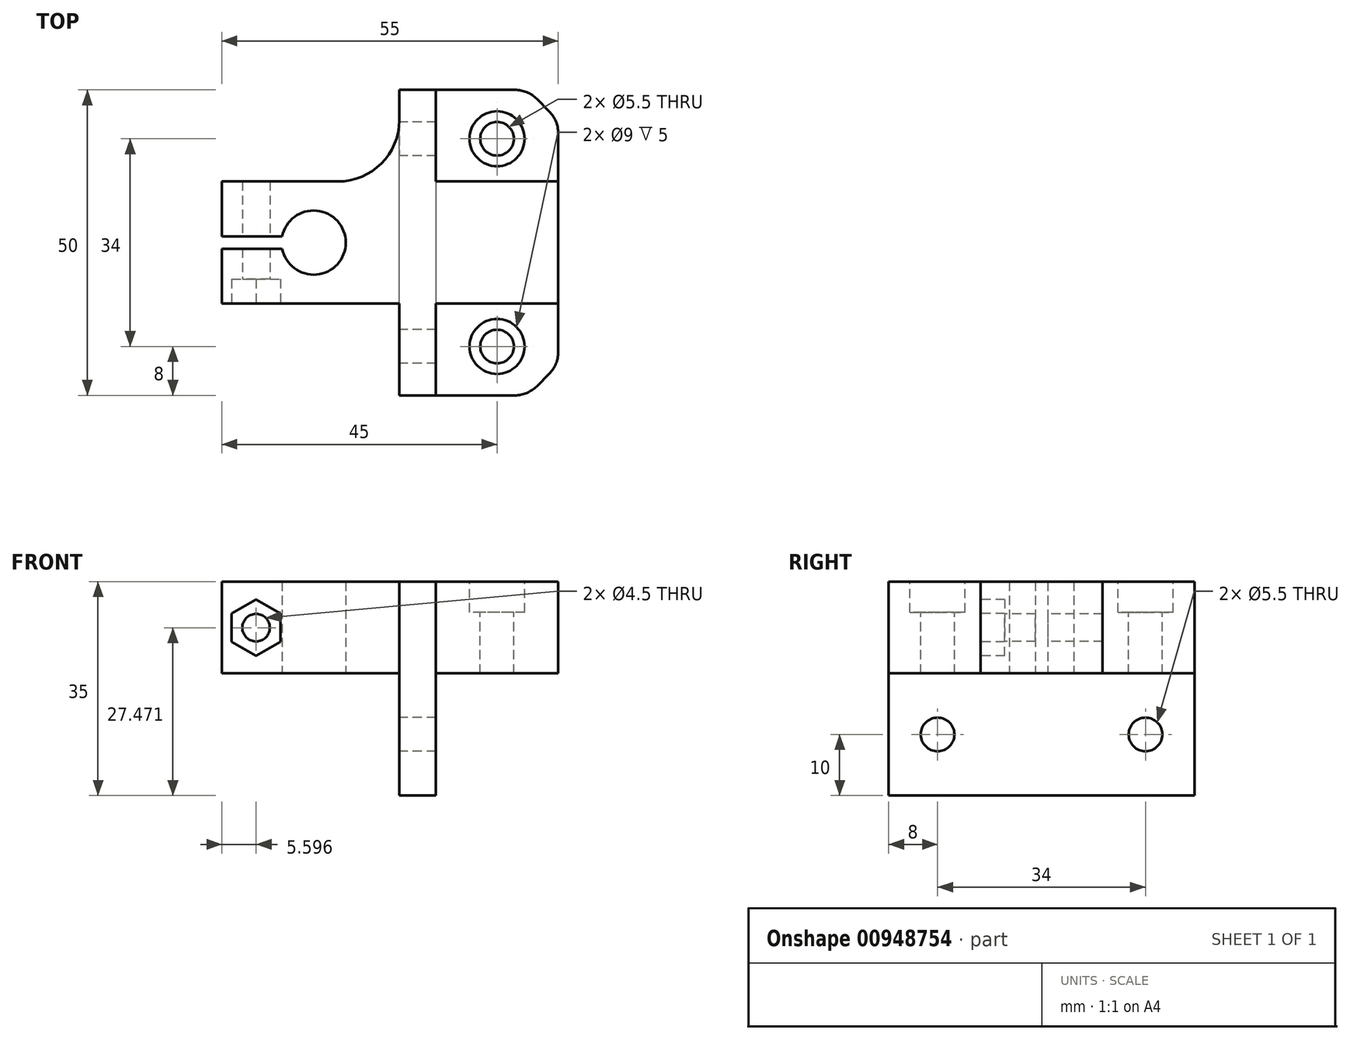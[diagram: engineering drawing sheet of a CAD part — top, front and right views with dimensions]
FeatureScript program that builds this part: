
annotation { "Feature Type Name" : "Feature", "Feature Type Description" : "" }
export const myFeature = defineFeature(function(context is Context, id is Id, definition is map)
    precondition{}
    {
        {
            var Q0;
            Q0=qCreatedBy(makeId("Top.planeOp"),FACE);
            var sketch = newSketch(context, id + "F0", { "sketchPlane" : qUnion([Q0])});
            skArc(sketch, "E0", {"start": v(-5.15, -1) * mm, "mid": v(5.25, 0) * mm, "end": v(-5.15, 1) * mm});
            skLineSegment(sketch, "E1", {"start": v(20, 0) * mm, "end": v(20, 25.4) * mm, "construction": true});
            skLineSegment(sketch, "E2", {"start": v(20, 0) * mm, "end": v(20, -26.33) * mm, "construction": true});
            skLineSegment(sketch, "E3", {"start": v(-15, 10) * mm, "end": v(40, 10) * mm});
            skLineSegment(sketch, "E4", {"start": v(-15, -10) * mm, "end": v(40, -10) * mm});
            skLineSegment(sketch, "E5", {"start": v(-15, 10) * mm, "end": v(-15, 1) * mm});
            skLineSegment(sketch, "E6", {"start": v(-15, 1) * mm, "end": v(-5.15, 1) * mm});
            skLineSegment(sketch, "E7", {"start": v(-15, -10) * mm, "end": v(-15, -1) * mm});
            skLineSegment(sketch, "E8", {"start": v(-15, -1) * mm, "end": v(-5.15, -1) * mm});
            skLineSegment(sketch, "E9", {"start": v(40, -10) * mm, "end": v(40, 10) * mm});
            skSolve(sketch);
        }
        {
            var Q0;
            Q0=qSketchRegion(id+"F0",true);
            extrude(context, id + "F1", {"entities" : qUnion([Q0]), "depth" : 15 * mm, "offsetDistance" : 25 * mm});
        }
        {
            var Q0;
            Q0=makeQuery(id+"F1.opExtrude","SWEPT_FACE",FACE,{"disambiguationData":[OSD([sQuery(id+"F0.wireOp",EDGE,"E4")])]});
            var sketch = newSketch(context, id + "F2", { "sketchPlane" : qUnion([Q0])});
            skLineSegment(sketch, "E10", {"start": v(20, 15) * mm, "end": v(20, 0) * mm});
            skLineSegment(sketch, "E11", {"start": v(20, 0) * mm, "end": v(14, 0) * mm});
            skLineSegment(sketch, "E12", {"start": v(14, 0) * mm, "end": v(14, 15) * mm});
            skLineSegment(sketch, "E13", {"start": v(14, 15) * mm, "end": v(20, 15) * mm});
            skSolve(sketch);
        }
        {
            var Q0;
            Q0=makeQuery(id+"F2.imprint","IMPRINT",FACE,{"disambiguationData":[TD([[makeQuery(id+"F2.imprint","IMPRINT",EDGE,{"derivedFrom":sQuery(id+"F2.wireOp",EDGE,"E10")}),-1.0]])]});
            extrude(context, id + "F3", {"entities" : qUnion([Q0]), "operationType" : NewBodyOperationType.ADD, "depth" : 15 * mm, "offsetDistance" : 25 * mm});
        }
        {
            var Q0;
            Q0=makeQuery(id+"F1.opExtrude","SWEPT_FACE",FACE,{"disambiguationData":[OSD([sQuery(id+"F0.wireOp",EDGE,"E3")])]});
            var sketch = newSketch(context, id + "F4", { "sketchPlane" : qUnion([Q0])});
            skLineSegment(sketch, "E14", {"start": v(-20, 15) * mm, "end": v(-20, 0) * mm});
            skLineSegment(sketch, "E15", {"start": v(-20, 0) * mm, "end": v(-14, 0) * mm});
            skLineSegment(sketch, "E16", {"start": v(-14, 0) * mm, "end": v(-14, 15) * mm});
            skLineSegment(sketch, "E17", {"start": v(-14, 15) * mm, "end": v(-20, 15) * mm});
            skSolve(sketch);
        }
        {
            var Q0;
            Q0=makeQuery(id+"F4.imprint","IMPRINT",FACE,{"disambiguationData":[TD([[makeQuery(id+"F4.imprint","IMPRINT",EDGE,{"derivedFrom":sQuery(id+"F4.wireOp",EDGE,"E14")}),1.0]])]});
            extrude(context, id + "F5", {"entities" : qUnion([Q0]), "operationType" : NewBodyOperationType.ADD, "depth" : 15 * mm, "offsetDistance" : 25 * mm});
        }
        {
            var Q0;
            Q0=makeQuery(id+"F5.boolean.opBoolean","MERGE",FACE,{"derivedFrom":[makeQuery(id+"F3.boolean.opBoolean","MERGE",FACE,{"derivedFrom":[makeQuery(id+"F1.opExtrude","CAP_FACE",FACE,{"disambiguationData":[OSD([sQuery(id+"F0.wireOp",EDGE,"E0"),sQuery(id+"F0.wireOp",EDGE,"E3"),sQuery(id+"F0.wireOp",EDGE,"E4"),sQuery(id+"F0.wireOp",EDGE,"E5"),sQuery(id+"F0.wireOp",EDGE,"E6"),sQuery(id+"F0.wireOp",EDGE,"E7"),sQuery(id+"F0.wireOp",EDGE,"E8"),sQuery(id+"F0.wireOp",EDGE,"E9")])],"isStart":true}),makeQuery(id+"F3.opExtrude","SWEPT_FACE",FACE,{"disambiguationData":[OSD([sQuery(id+"F2.wireOp",EDGE,"E11")])]})]}),makeQuery(id+"F5.opExtrude","SWEPT_FACE",FACE,{"disambiguationData":[OSD([sQuery(id+"F4.wireOp",EDGE,"E15")])]})]});
            var sketch = newSketch(context, id + "F6", { "sketchPlane" : qUnion([Q0])});
            skLineSegment(sketch, "E18.bottom", {"start": v(14, 25) * mm, "end": v(20, 25) * mm});
            skLineSegment(sketch, "E18.top", {"start": v(14, -25) * mm, "end": v(20, -25) * mm});
            skLineSegment(sketch, "E18.left", {"start": v(14, 25) * mm, "end": v(14, -25) * mm});
            skLineSegment(sketch, "E18.right", {"start": v(20, 25) * mm, "end": v(20, -25) * mm});
            skSolve(sketch);
        }
        {
            var Q0;
            Q0=qSketchRegion(id+"F6",true);
            extrude(context, id + "F7", {"entities" : qUnion([Q0]), "operationType" : NewBodyOperationType.ADD, "depth" : 20 * mm, "offsetDistance" : 25 * mm});
        }
        {
            var Q0;
            Q0=makeQuery(id+"F7.boolean.opBoolean","MERGE",FACE,{"derivedFrom":[makeQuery(id+"F3.opExtrude","SWEPT_FACE",FACE,{"disambiguationData":[OSD([sQuery(id+"F2.wireOp",EDGE,"E12")])]}),makeQuery(id+"F5.opExtrude","SWEPT_FACE",FACE,{"disambiguationData":[OSD([sQuery(id+"F4.wireOp",EDGE,"E16")])]}),makeQuery(id+"F7.opExtrude","SWEPT_FACE",FACE,{"disambiguationData":[OSD([sQuery(id+"F6.wireOp",EDGE,"E18.left")])]})]});
            var sketch = newSketch(context, id + "F8", { "sketchPlane" : qUnion([Q0])});
            skCircle(sketch, "E19", {"center": v(-17, -10) * mm, "radius": 2.75 * mm});
            skCircle(sketch, "E20", {"center": v(17, -10) * mm, "radius": 2.75 * mm});
            skSolve(sketch);
        }
        {
            var Q0;
            Q0=makeQuery(id+"F8.imprint","IMPRINT",FACE,{"disambiguationData":[TD([[makeQuery(id+"F8.imprint","IMPRINT",EDGE,{"derivedFrom":sQuery(id+"F8.wireOp",EDGE,"E19")}),1.0]])]});
            var Q1;
            Q1=makeQuery(id+"F8.imprint","IMPRINT",FACE,{"disambiguationData":[TD([[makeQuery(id+"F8.imprint","IMPRINT",EDGE,{"derivedFrom":sQuery(id+"F8.wireOp",EDGE,"E20")}),1.0]])]});
            extrude(context, id + "F9", {"entities" : qUnion([Q0, Q1]), "operationType" : NewBodyOperationType.REMOVE, "oppositeDirection" : true, "depth" : 10 * mm, "offsetDistance" : 25 * mm});
        }
        {
            var Q0;
            Q0=makeQuery(id+"F5.boolean.opBoolean","MERGE",FACE,{"derivedFrom":[makeQuery(id+"F3.boolean.opBoolean","MERGE",FACE,{"derivedFrom":[makeQuery(id+"F1.opExtrude","CAP_FACE",FACE,{"disambiguationData":[OSD([sQuery(id+"F0.wireOp",EDGE,"E0"),sQuery(id+"F0.wireOp",EDGE,"E3"),sQuery(id+"F0.wireOp",EDGE,"E4"),sQuery(id+"F0.wireOp",EDGE,"E5"),sQuery(id+"F0.wireOp",EDGE,"E6"),sQuery(id+"F0.wireOp",EDGE,"E7"),sQuery(id+"F0.wireOp",EDGE,"E8"),sQuery(id+"F0.wireOp",EDGE,"E9")])],"isStart":false}),makeQuery(id+"F3.opExtrude","SWEPT_FACE",FACE,{"disambiguationData":[OSD([sQuery(id+"F2.wireOp",EDGE,"E13")])]})]}),makeQuery(id+"F5.opExtrude","SWEPT_FACE",FACE,{"disambiguationData":[OSD([sQuery(id+"F4.wireOp",EDGE,"E17")])]})]});
            var sketch = newSketch(context, id + "F10", { "sketchPlane" : qUnion([Q0])});
            skLineSegment(sketch, "E21", {"start": v(20, 10) * mm, "end": v(20, 25) * mm});
            skLineSegment(sketch, "E22", {"start": v(20, 25) * mm, "end": v(35, 25) * mm});
            skLineSegment(sketch, "E23", {"start": v(40, 10) * mm, "end": v(40, 20) * mm});
            skLineSegment(sketch, "E24", {"start": v(40, 20) * mm, "end": v(35, 25) * mm});
            skLineSegment(sketch, "E25", {"start": v(20, -10) * mm, "end": v(20, -25) * mm});
            skLineSegment(sketch, "E26", {"start": v(20, -25) * mm, "end": v(35, -25) * mm});
            skLineSegment(sketch, "E27", {"start": v(40, -10) * mm, "end": v(40, -20) * mm});
            skLineSegment(sketch, "E28", {"start": v(40, -20) * mm, "end": v(35, -25) * mm});
            skSolve(sketch);
        }
        {
            var Q0;
            Q0=makeQuery(id+"F10.imprint","IMPRINT",FACE,{"disambiguationData":[TD([[makeQuery(id+"F10.imprint","IMPRINT",EDGE,{"derivedFrom":sQuery(id+"F10.wireOp",EDGE,"E21")}),1.0]])]});
            var Q1;
            Q1=makeQuery(id+"F10.imprint","IMPRINT",FACE,{"disambiguationData":[TD([[makeQuery(id+"F10.imprint","IMPRINT",EDGE,{"derivedFrom":sQuery(id+"F10.wireOp",EDGE,"E25")}),-1.0]])]});
            extrude(context, id + "F11", {"entities" : qUnion([Q0, Q1]), "oppositeDirection" : true, "depth" : 15 * mm, "offsetDistance" : 25 * mm});
        }
        {
            var Q0;
            Q0=makeQuery(id+"F3.opExtrude","CAP_EDGE",EDGE,{"disambiguationData":[OSD([sQuery(id+"F2.wireOp",EDGE,"E12")])],"isStart":true});
            var Q1;
            Q1=makeQuery(id+"F5.opExtrude","CAP_EDGE",EDGE,{"disambiguationData":[OSD([sQuery(id+"F4.wireOp",EDGE,"E16")])],"isStart":true});
            fillet(context, id + "F12", {"entities" : qUnion([Q0, Q1]), "radius" : 10 * mm, "tangentPropagation" : true, "allowEdgeOverflow" : false});
        }
        {
            var Q0;
            Q0=makeQuery(id+"F11.opExtrude","SWEPT_EDGE",EDGE,{"disambiguationData":[OSD([sQuery(id+"F10.wireOp",EDGE,"E26"),sQuery(id+"F10.wireOp",EDGE,"E28")])]});
            var Q1;
            Q1=makeQuery(id+"F11.opExtrude","SWEPT_EDGE",EDGE,{"disambiguationData":[OSD([sQuery(id+"F10.wireOp",EDGE,"E27"),sQuery(id+"F10.wireOp",EDGE,"E28")])]});
            var Q2;
            Q2=makeQuery(id+"F11.opExtrude","SWEPT_EDGE",EDGE,{"disambiguationData":[OSD([sQuery(id+"F10.wireOp",EDGE,"E23"),sQuery(id+"F10.wireOp",EDGE,"E24")])]});
            var Q3;
            Q3=makeQuery(id+"F11.opExtrude","SWEPT_EDGE",EDGE,{"disambiguationData":[OSD([sQuery(id+"F10.wireOp",EDGE,"E22"),sQuery(id+"F10.wireOp",EDGE,"E24")])]});
            fillet(context, id + "F13", {"entities" : qUnion([Q0, Q1, Q2, Q3]), "radius" : 5 * mm, "tangentPropagation" : true, "allowEdgeOverflow" : false});
        }
        {
            var Q0;
            {var subQ0=sQuery(id+"F0.wireOp",EDGE,"E7");var subQ5=sQuery(id+"F0.wireOp",EDGE,"E4");Q0=makeQuery(id+"F3.boolean.opBoolean","SPLIT",FACE,{"disambiguationData":[TD([makeQuery(id+"F1.opExtrude","SWEPT_FACE",FACE,{"disambiguationData":[OSD([subQ0])]})])],"derivedFrom":makeQuery(id+"F1.opExtrude","SWEPT_FACE",FACE,{"disambiguationData":[OSD([subQ5])]})});}
            var sketch = newSketch(context, id + "F14", { "sketchPlane" : qUnion([Q0])});
            skCircle(sketch, "E29", {"center": v(-9.4, 7.47) * mm, "radius": 2.25 * mm});
            skLineSegment(sketch, "E30.0", {"start": v(-5.4, 9.78) * mm, "end": v(-5.4, 5.16) * mm});
            skLineSegment(sketch, "E30.1", {"start": v(-5.4, 5.16) * mm, "end": v(-9.4, 2.85) * mm});
            skLineSegment(sketch, "E30.2", {"start": v(-9.4, 2.85) * mm, "end": v(-13.4, 5.16) * mm});
            skLineSegment(sketch, "E30.3", {"start": v(-13.4, 5.16) * mm, "end": v(-13.4, 9.78) * mm});
            skLineSegment(sketch, "E30.4", {"start": v(-13.4, 9.78) * mm, "end": v(-9.4, 12.09) * mm});
            skLineSegment(sketch, "E30.5", {"start": v(-9.4, 12.09) * mm, "end": v(-5.4, 9.78) * mm});
            skPoint(sketch, "E30.0.midPoint", {"position": v(-5.4, 7.47) * mm});
            skSolve(sketch);
        }
        {
            var Q0;
            Q0=makeQuery(id+"F14.imprint","IMPRINT",FACE,{"disambiguationData":[TD([[makeQuery(id+"F14.imprint","IMPRINT",EDGE,{"derivedFrom":sQuery(id+"F14.wireOp",EDGE,"E29")}),1.0]])]});
            extrude(context, id + "F15", {"entities" : qUnion([Q0]), "operationType" : NewBodyOperationType.REMOVE, "oppositeDirection" : true, "depth" : 25 * mm, "offsetDistance" : 25 * mm});
        }
        {
            var Q0;
            Q0=makeQuery(id+"F14.imprint","IMPRINT",FACE,{"disambiguationData":[TD([[makeQuery(id+"F14.imprint","IMPRINT",EDGE,{"derivedFrom":sQuery(id+"F14.wireOp",EDGE,"E29")}),-1.0]])]});
            extrude(context, id + "F16", {"entities" : qUnion([Q0]), "operationType" : NewBodyOperationType.REMOVE, "oppositeDirection" : true, "depth" : 4 * mm, "offsetDistance" : 25 * mm});
        }
        {
            var Q0;
            Q0=makeQuery(id+"F11.opExtrude","CAP_FACE",FACE,{"disambiguationData":[OSD([sQuery(id+"F0.wireOp",EDGE,"E3"),sQuery(id+"F10.wireOp",EDGE,"E21"),sQuery(id+"F10.wireOp",EDGE,"E22"),sQuery(id+"F10.wireOp",EDGE,"E23"),sQuery(id+"F10.wireOp",EDGE,"E24")])],"isStart":true});
            var sketch = newSketch(context, id + "F17", { "sketchPlane" : qUnion([Q0])});
            skCircle(sketch, "E31", {"center": v(30, 17) * mm, "radius": 2.75 * mm});
            skCircle(sketch, "E32", {"center": v(30, 17) * mm, "radius": 4.5 * mm});
            skSolve(sketch);
        }
        {
            var Q0;
            Q0=makeQuery(id+"F17.imprint","IMPRINT",FACE,{"disambiguationData":[TD([[makeQuery(id+"F17.imprint","IMPRINT",EDGE,{"derivedFrom":sQuery(id+"F17.wireOp",EDGE,"E31")}),1.0]])]});
            extrude(context, id + "F18", {"entities" : qUnion([Q0]), "operationType" : NewBodyOperationType.REMOVE, "oppositeDirection" : true, "depth" : 20 * mm, "offsetDistance" : 25 * mm});
        }
        {
            var Q0;
            Q0=makeQuery(id+"F17.imprint","IMPRINT",FACE,{"disambiguationData":[TD([[makeQuery(id+"F17.imprint","IMPRINT",EDGE,{"derivedFrom":sQuery(id+"F17.wireOp",EDGE,"E31")}),-1.0]])]});
            extrude(context, id + "F19", {"entities" : qUnion([Q0]), "operationType" : NewBodyOperationType.REMOVE, "oppositeDirection" : true, "depth" : 5 * mm, "offsetDistance" : 25 * mm});
        }
        {
            var Q0;
            Q0=makeQuery(id+"F11.opExtrude","CAP_FACE",FACE,{"disambiguationData":[OSD([sQuery(id+"F0.wireOp",EDGE,"E4"),sQuery(id+"F10.wireOp",EDGE,"E25"),sQuery(id+"F10.wireOp",EDGE,"E26"),sQuery(id+"F10.wireOp",EDGE,"E27"),sQuery(id+"F10.wireOp",EDGE,"E28")])],"isStart":true});
            var sketch = newSketch(context, id + "F20", { "sketchPlane" : qUnion([Q0])});
            skCircle(sketch, "E33", {"center": v(30, -17) * mm, "radius": 2.75 * mm});
            skCircle(sketch, "E34", {"center": v(30, -17) * mm, "radius": 4.5 * mm});
            skSolve(sketch);
        }
        {
            var Q0;
            Q0=makeQuery(id+"F20.imprint","IMPRINT",FACE,{"disambiguationData":[TD([[makeQuery(id+"F20.imprint","IMPRINT",EDGE,{"derivedFrom":sQuery(id+"F20.wireOp",EDGE,"E33")}),1.0]])]});
            extrude(context, id + "F21", {"entities" : qUnion([Q0]), "operationType" : NewBodyOperationType.REMOVE, "oppositeDirection" : true, "depth" : 20 * mm, "offsetDistance" : 25 * mm});
        }
        {
            var Q0;
            Q0=makeQuery(id+"F20.imprint","IMPRINT",FACE,{"disambiguationData":[TD([[makeQuery(id+"F20.imprint","IMPRINT",EDGE,{"derivedFrom":sQuery(id+"F20.wireOp",EDGE,"E33")}),-1.0]])]});
            extrude(context, id + "F22", {"entities" : qUnion([Q0]), "operationType" : NewBodyOperationType.REMOVE, "oppositeDirection" : true, "depth" : 5 * mm, "offsetDistance" : 25 * mm});
        }
    });
